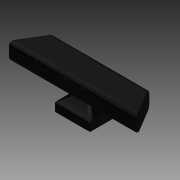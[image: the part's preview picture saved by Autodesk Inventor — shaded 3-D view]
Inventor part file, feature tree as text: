
AUTODESK INVENTOR PART (.ipt)
format: ipt  version: 2018 (Build 220112000, 112)  size: 527,872 bytes
history: native  units: in
note: dims shown in document units (in); Inventor stores cm internally (conversion verified against a paired STEP export)
features: fillet x8, extrude x7, sketch x7, plane x1, projected_geometry x1
ambient origin geometry x8: Origin, YZ Plane, XZ Plane, XY Plane, X Axis, Y Axis, Z Axis, Center Point
bodies: Solid1 (feature_tree)
feature tree (24):
  extrude  "Extrusion1"  Depth=1.5in
  extrude  "Extrusion2"  Depth=11.0in
  extrude  "Extrusion3"  Depth=0.25in
  fillet  "Fillet3"  Radius=2.5in
  fillet  "Fillet1"  Radius=1.5in
  extrude  "Extrusion4"  Depth=2.5625in TaperAngle=0.0deg
  extrude  "Extrusion5"  Depth=0.375in
  plane  "Work Plane1"
  extrude  "Extrusion6"  Depth=1.0in
  fillet  "Fillet6"  Radius=1.0in
  extrude  "Extrusion7"  Depth=0.1in
  fillet  "Fillet7"  Radius=1.0in
  fillet  "Fillet8"  Radius=1.125in
  fillet  "Fillet9"  Radius=0.0312in
  fillet  "Fillet10"  Radius=0.875in
  fillet  "Fillet11"  Radius=0.625in
  sketch  "Sketch1"  dims[d2=3.0in d3=1.5in]
  sketch  "Sketch2"  dims[d4=3.0in d5=0.0in d6=11.0in]
  sketch  "Sketch3"  dims[d7=1.5in d8=0.25in d9=2.5in d10=0.0in d11=1.5in]
  sketch  "Sketch4"  dims[d12=1.5in d13=2.5625in d14=0.0in]
  sketch  "Sketch5"  dims[d15=0.125in d17=0.375in]
  sketch  "Sketch7"  dims[d18=0.75in d19=1.0in d20=1.0in]
  projected_geometry  "Projected Loop1"
  sketch  "Sketch8"  dims[d21=1.5in d22=0.0in d23=1.0in d24=1.0in d25=1.125in d26=0.0in d31=0.0312in d32=0.875in d33=0.625in d34=0.0in d35=0.02in d36=0.25in d37=1.0in d38=0.0in d39=0.5in d40=0.1in d41=0.1in d42=0.1in d43=0.1in]
